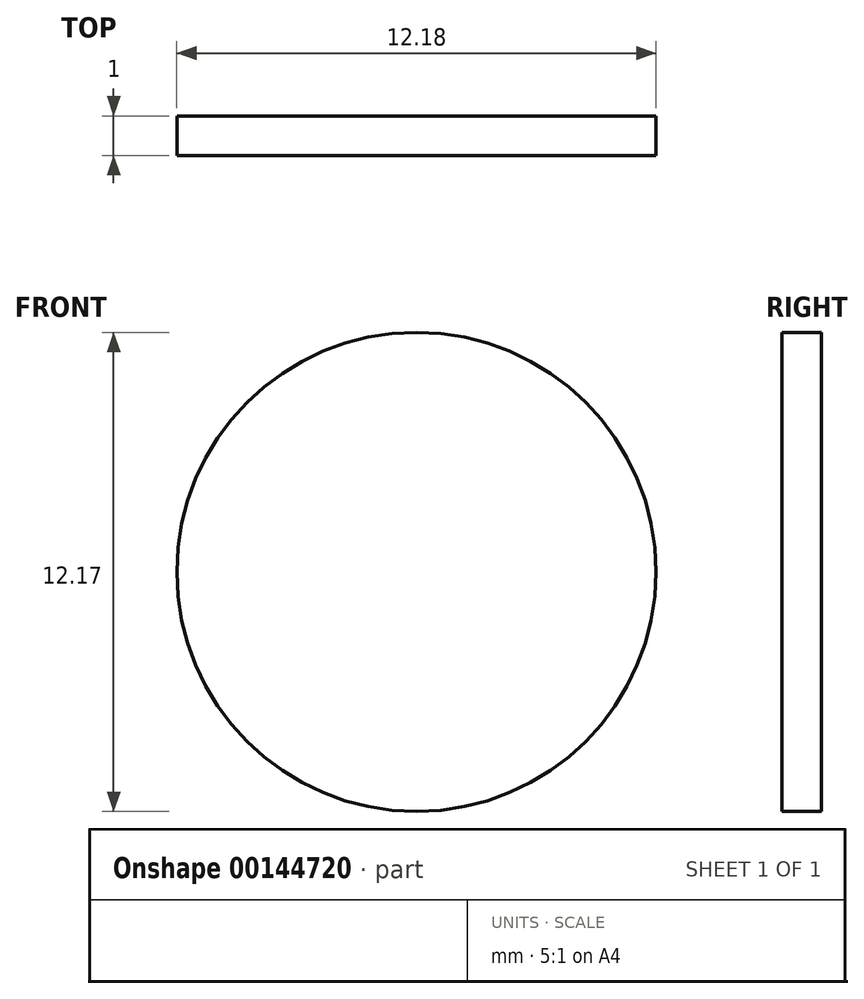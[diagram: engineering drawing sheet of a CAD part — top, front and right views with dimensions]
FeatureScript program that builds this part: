
annotation { "Feature Type Name" : "Feature", "Feature Type Description" : "" }
export const myFeature = defineFeature(function(context is Context, id is Id, definition is map)
    precondition{}
    {
        {
            var Q0;
            Q0=qCreatedBy(makeId("Front.planeOp"),FACE);
            var sketch = newSketch(context, id + "F0", { "sketchPlane" : qUnion([Q0])});
            skCircle(sketch, "E0", {"center": v(-19.58, 41.19) * mm, "radius": 6.09 * mm});
            skSolve(sketch);
        }
        {
            var Q0;
            Q0=makeQuery(id+"F0.imprint","IMPRINT",FACE,{"disambiguationData":[TD([[makeQuery(id+"F0.imprint","IMPRINT",EDGE,{"derivedFrom":sQuery(id+"F0.wireOp",EDGE,"E0")}),1.0]])]});
            extrude(context, id + "F1", {"entities" : qUnion([Q0]), "depth" : 1 * mm});
        }
    });
